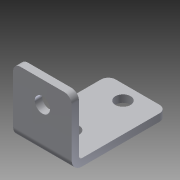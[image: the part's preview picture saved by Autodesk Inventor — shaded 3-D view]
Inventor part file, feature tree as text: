
AUTODESK INVENTOR PART (.ipt)
format: ipt  version: 2013 (Build 170138000, 138)  size: 185,344 bytes
history: native  units: in
note: dims shown in document units (in); Inventor stores cm internally (conversion verified against a paired STEP export)
features: sheet_metal_op x4, other x4, sketch x3, chamfer x1
ambient origin geometry x8: Origin, YZ Plane, XZ Plane, XY Plane, X Axis, Y Axis, Z Axis, Center Point
feature tree (12):
  sheet_metal_op  "Face1"
  sheet_metal_op  "Flange1"
  chamfer  "Corner Round1"
  sketch  "Sketch1"  dims[d1=1.0in]
  other  "Plate1"
  sketch  "Sketch2"  dims[d2=0.26in]
  other  "Plate2"
  sheet_metal_op  "Bend1"
  sheet_metal_op  "Corner1"
  sketch  "Sketch3"  dims[d3=0.26in d4=0.875in d8=0.125in d9=0.125in d10=0.0625in d11=0.25in d12=0.125in d13=1.125in d14=90.0deg d15=0.05in d16=0.5in d17=0.125in d18=0.125in d19=0.26in d21=0.75in d22=0.125in d23=0.0in d24=0.125in d25=0.5in d26=0.25in d0=0.25in d5=0.125in d6=0.0in]
  other  "Cut1"
  other  "Definition1"
